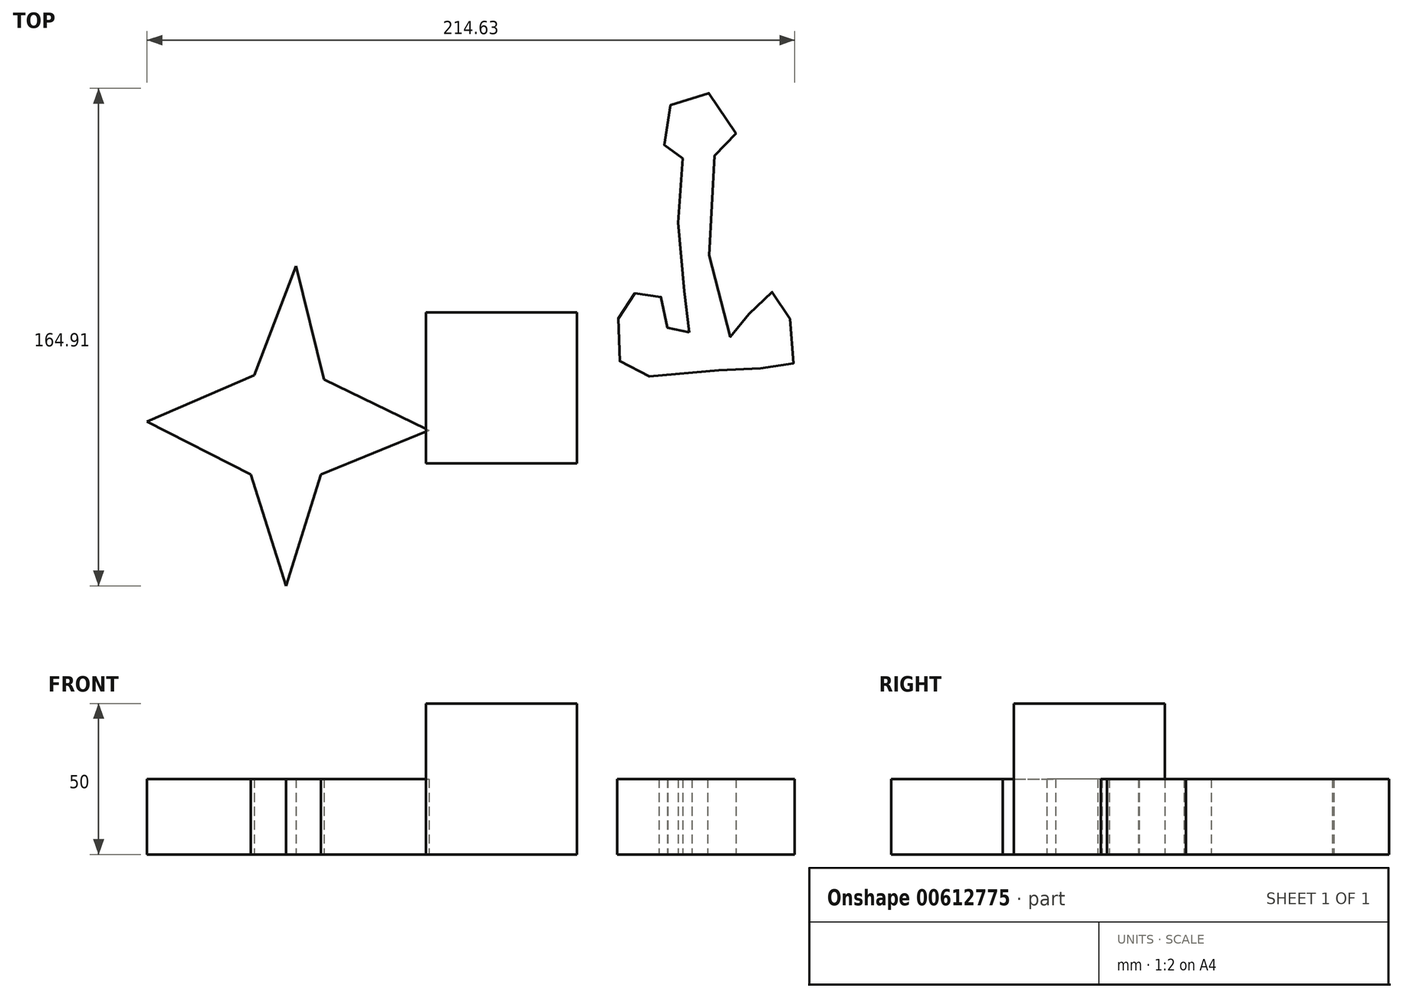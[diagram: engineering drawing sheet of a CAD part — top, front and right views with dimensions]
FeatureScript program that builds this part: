
annotation { "Feature Type Name" : "Feature", "Feature Type Description" : "" }
export const myFeature = defineFeature(function(context is Context, id is Id, definition is map)
    precondition{}
    {
        {
            var Q0;
            Q0=qCreatedBy(makeId("Top.planeOp"),FACE);
            var sketch = newSketch(context, id + "F0", { "sketchPlane" : qUnion([Q0])});
            skLineSegment(sketch, "E0.bottom", {"start": v(25, 25) * mm, "end": v(-25, 25) * mm});
            skLineSegment(sketch, "E0.top", {"start": v(25, -25) * mm, "end": v(-25, -25) * mm});
            skLineSegment(sketch, "E0.left", {"start": v(25, 25) * mm, "end": v(25, -25) * mm});
            skLineSegment(sketch, "E0.right", {"start": v(-25, 25) * mm, "end": v(-25, -25) * mm});
            skPoint(sketch, "E0.middle", {"position": v(0, 0) * mm});
            skSolve(sketch);
        }
        {
            var Q0;
            Q0 = qSketchRegion(id + "F0", true);
            extrude(context, id + "F1", {"entities" : qUnion([Q0]), "depth" : 50 * mm, "offsetDistance" : 25 * mm});
        }
        {
            var Q0;
            Q0=qCreatedBy(makeId("Top.planeOp"),FACE);
            var sketch = newSketch(context, id + "F2", { "sketchPlane" : qUnion([Q0])});
            skFitSpline(sketch, "E1", {"points": [v(62.29, 18.4) * mm, v(60.94, 30.93) * mm, v(59.16, 66.69) * mm, v(58.7, 81) * mm, v(52.9, 81) * mm, v(58.7, 97.09) * mm, v(70.78, 96.2) * mm, v(77.48, 82.78) * mm, v(71.67, 79.2) * mm, v(75.25, 17.51) * mm, v(81.06, 18.85) * mm, v(83.74, 30.48) * mm, v(93.13, 30.48) * mm, v(95.81, 21.09) * mm, v(96.26, 7.23) * mm, v(86.87, 6.34) * mm, v(76.6, 6.34) * mm, v(44.85, 4.1) * mm, v(39.49, 8.13) * mm, v(38.6, 21.54) * mm, v(41.72, 30.48) * mm, v(47.53, 31.37) * mm, v(52.45, 30.48) * mm, v(55.13, 25.12) * mm, v(56.03, 17.07) * mm, v(62.29, 18.4) * mm]});
            skSolve(sketch);
        }
        {
            var Q0;
            Q0 = qSketchRegion(id + "F2", true);
            var Q1;
            Q1 = qConstructionFilter(qBodyType(qCreatedBy(id + "F2" ,EDGE), BodyType.WIRE), ConstructionObject.NO);
            extrude(context, id + "F3", {"entities" : qUnion([Q0]), "surfaceEntities" : qUnion([Q1]), "depth" : 25 * mm, "offsetDistance" : 25 * mm});
        }
        {
            var Q0;
            Q0=qCreatedBy(makeId("Top.planeOp"),FACE);
            var sketch = newSketch(context, id + "F4", { "sketchPlane" : qUnion([Q0])});
            skLineSegment(sketch, "E2", {"start": v(-82.96, -28.7) * mm, "end": v(-71.39, -65.6) * mm});
            skLineSegment(sketch, "E3", {"start": v(-71.39, -65.6) * mm, "end": v(-59.74, -28.73) * mm});
            skLineSegment(sketch, "E4", {"start": v(-59.74, -28.73) * mm, "end": v(-23.95, -14.07) * mm});
            skLineSegment(sketch, "E5", {"start": v(-82.96, -28.7) * mm, "end": v(-117.41, -11.11) * mm});
            skLineSegment(sketch, "E6", {"start": v(-117.41, -11.11) * mm, "end": v(-23.95, -14.07) * mm});
            skLineSegment(sketch, "E7.MirrorCS", {"start": v(-68.04, 40.37) * mm, "end": v(-58.74, 2.83) * mm});
            skLineSegment(sketch, "E8.MirrorCS", {"start": v(-81.92, 4.27) * mm, "end": v(-68.04, 40.37) * mm});
            skLineSegment(sketch, "E9.MirrorCS", {"start": v(-58.74, 2.83) * mm, "end": v(-23.95, -14.07) * mm});
            skLineSegment(sketch, "E10.MirrorCS", {"start": v(-81.92, 4.27) * mm, "end": v(-117.41, -11.11) * mm});
            skSolve(sketch);
        }
        {
            var Q0;
            Q0=makeQuery(id+"F4.imprint","IMPRINT",FACE,{"disambiguationData":[TD([[makeQuery(id+"F4.imprint","IMPRINT",EDGE,{"derivedFrom":sQuery(id+"F4.wireOp",EDGE,"E2")}),1.0]])]});
            var Q1;
            Q1=makeQuery(id+"F4.imprint","IMPRINT",FACE,{"disambiguationData":[TD([[makeQuery(id+"F4.imprint","IMPRINT",EDGE,{"derivedFrom":sQuery(id+"F4.wireOp",EDGE,"E6")}),1.0]])]});
            extrude(context, id + "F5", {"entities" : qUnion([Q0, Q1]), "depth" : 25 * mm, "offsetDistance" : 25 * mm});
        }
    });
